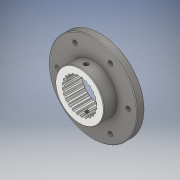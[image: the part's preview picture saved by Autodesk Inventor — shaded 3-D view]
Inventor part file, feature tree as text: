
AUTODESK INVENTOR PART (.ipt)
format: ipt  version: 2019 (Build 230136000, 136)  size: 393,728 bytes
history: native  units: in
note: dims shown in document units (in); Inventor stores cm internally (conversion verified against a paired STEP export)
features: sketch x5, hole x3, extrude x2, fillet x2, imported_body x1
ambient origin geometry x8: Origin, YZ Plane, XZ Plane, XY Plane, X Axis, Y Axis, Z Axis, Center Point
bodies: Solid1 (feature_tree)
feature tree (13):
  extrude  "Extrusion2"  Depth=0.75in TaperAngle=0.0deg
  hole  "Hole1"  [1 undecoded]
  fillet  "Fillet1"  Radius=4.0in
  hole  "Hole3"  [1 undecoded]
  hole  "Hole4"  [1 undecoded]
  extrude  "Extrusion3"  [1 undecoded]
  fillet  "Fillet2"  [1 undecoded]
  sketch  "Sketch1"  dims[d0=2.75in d3=0.75in d4=0.0in]
  sketch  "Sketch3"  dims[d5=0.196in d6=1.5748in d7=0.1575in d8=0.0787in d9=90.0deg d10=1771.6535in d11=0.8108in d12=0.0394in d20=4.0in]
  sketch  "Sketch5"  dims[d21=0.266in d22=1.5748in d23=0.507in d24=0.0787in d25=0.563in d26=1771.6535in d27=0.8108in]
  sketch  "Sketch7"  dims[d28=0.252in d29=1.378in d30=0.507in d31=0.0787in d32=0.563in d33=1.5748in d34=0.8108in d35=5.0in]
  sketch  "Sketch8"  dims[d36=0.75in d37=0.0in d38=0.0394in]
  imported_body  "Base1"
note: 5 required parameter values undecoded (feature->parameter linkage not recoverable at this tier; creation-order binding heuristic only, values carry confidence <= 0.55)
